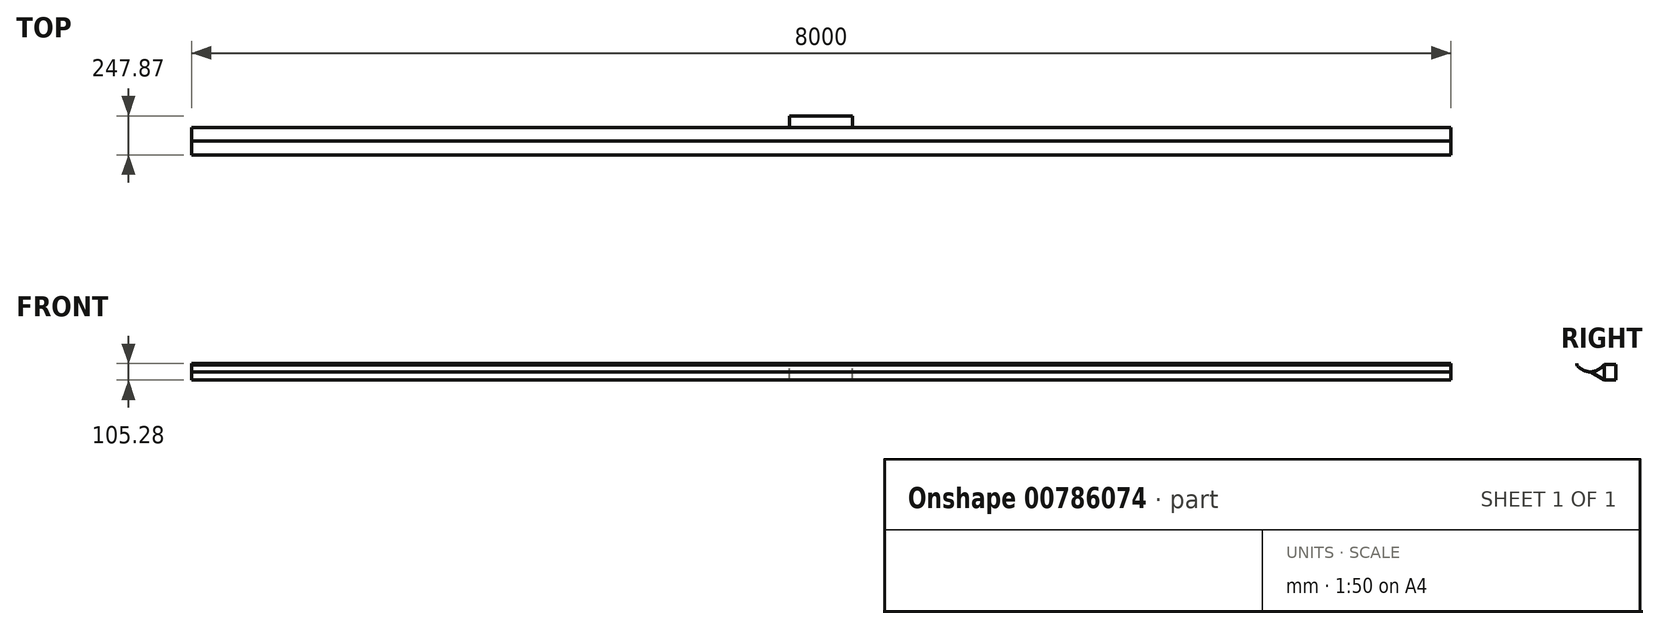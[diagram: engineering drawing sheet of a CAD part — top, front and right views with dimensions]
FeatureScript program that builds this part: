
annotation { "Feature Type Name" : "Feature", "Feature Type Description" : "" }
export const myFeature = defineFeature(function(context is Context, id is Id, definition is map)
    precondition{}
    {
        {
            var Q0;
            Q0=qCreatedBy(makeId("Right.planeOp"),FACE);
            var sketch = newSketch(context, id + "F0", { "sketchPlane" : qUnion([Q0])});
            skArc(sketch, "E0", {"start": v(-87.67, 11.49) * mm, "mid": v(0, -31.44) * mm, "end": v(85.2, 16.2) * mm});
            skLineSegment(sketch, "E1", {"start": v(-87.67, 11.49) * mm, "end": v(-87.67, 21.49) * mm});
            skLineSegment(sketch, "E2", {"start": v(0, -31.44) * mm, "end": v(85.2, -83.8) * mm});
            skLineSegment(sketch, "E3", {"start": v(85.2, -83.8) * mm, "end": v(85.2, 16.2) * mm});
            skLineSegment(sketch, "E4", {"start": v(0, -31.44) * mm, "end": v(85.2, -31.44) * mm});
            skPoint(sketch, "E4.endSnap0", {"position": v(85.2, -33.8) * mm});
            skLineSegment(sketch, "E5", {"start": v(41.06, -21.87) * mm, "end": v(41.06, -56.67) * mm});
            skLineSegment(sketch, "E6", {"start": v(54.68, -14.34) * mm, "end": v(54.68, -65.04) * mm});
            skLineSegment(sketch, "E7", {"start": v(66.2, -5.62) * mm, "end": v(66.2, -72.12) * mm});
            skLineSegment(sketch, "E8", {"start": v(85.2, -83.8) * mm, "end": v(160.2, -83.8) * mm});
            skLineSegment(sketch, "E9", {"start": v(110.2, -83.8) * mm, "end": v(110.2, 16.2) * mm});
            skLineSegment(sketch, "E10", {"start": v(135.2, -83.8) * mm, "end": v(135.2, 16.2) * mm});
            skLineSegment(sketch, "E11", {"start": v(160.2, -83.8) * mm, "end": v(160.2, 16.2) * mm});
            skLineSegment(sketch, "E12", {"start": v(85.2, 16.2) * mm, "end": v(110.2, 16.2) * mm});
            skLineSegment(sketch, "E13", {"start": v(135.2, 16.2) * mm, "end": v(110.2, 16.2) * mm});
            skLineSegment(sketch, "E14", {"start": v(160.2, 16.2) * mm, "end": v(135.2, 16.2) * mm});
            skLineSegment(sketch, "E15", {"start": v(76.2, 4.34) * mm, "end": v(76.2, -78.26) * mm});
            skLineSegment(sketch, "E16", {"start": v(85.2, -5.22) * mm, "end": v(110.2, -5.22) * mm});
            skLineSegment(sketch, "E17", {"start": v(110.2, -5.22) * mm, "end": v(123.7, -5.22) * mm});
            skLineSegment(sketch, "E18", {"start": v(123.7, -5.22) * mm, "end": v(123.7, -15.48) * mm});
            skLineSegment(sketch, "E19", {"start": v(123.7, -15.48) * mm, "end": v(160.2, -15.48) * mm});
            skLineSegment(sketch, "E20", {"start": v(123.7, -5.22) * mm, "end": v(123.7, 16.2) * mm});
            skLineSegment(sketch, "E21", {"start": v(85.2, 6.9) * mm, "end": v(123.7, 6.9) * mm});
            skLineSegment(sketch, "E22", {"start": v(160.2, -31.4) * mm, "end": v(85.2, -31.4) * mm});
            skLineSegment(sketch, "E23", {"start": v(123.7, -15.48) * mm, "end": v(85.2, -15.48) * mm});
            skLineSegment(sketch, "E24", {"start": v(85.2, -23.07) * mm, "end": v(160.2, -23.07) * mm});
            skLineSegment(sketch, "E25", {"start": v(85.2, -39.16) * mm, "end": v(160.2, -39.16) * mm});
            skLineSegment(sketch, "E26", {"start": v(85.2, -48.32) * mm, "end": v(160.2, -48.32) * mm});
            skLineSegment(sketch, "E27", {"start": v(85.2, -56.67) * mm, "end": v(160.2, -56.67) * mm});
            skLineSegment(sketch, "E28", {"start": v(85.2, -66.65) * mm, "end": v(160.2, -66.65) * mm});
            skLineSegment(sketch, "E29", {"start": v(85.2, -74.19) * mm, "end": v(160.2, -74.19) * mm});
            skSolve(sketch);
        }
        {
            var Q0;
            Q0=sQuery(id+"F0.wireOp",EDGE,"E2");
            extrude(context, id + "F1", {"bodyType" : ToolBodyType.SURFACE, "surfaceEntities" : qUnion([Q0]), "endBound" : BoundingType.SYMMETRIC, "depth" : 8000 * mm, "offsetDistance" : 25.4 * mm});
        }
        {
            var Q0;
            Q0=sQuery(id+"F0.wireOp",EDGE,"E0");
            var Q1;
            Q1=sQuery(id+"F0.wireOp",EDGE,"E1");
            extrude(context, id + "F2", {"bodyType" : ToolBodyType.SURFACE, "surfaceEntities" : qUnion([Q0, Q1]), "endBound" : BoundingType.SYMMETRIC, "depth" : 8000 * mm, "offsetDistance" : 25.4 * mm});
        }
        {
            var Q0;
            Q0=sQuery(id+"F0.wireOp",EDGE,"E12");
            var Q1;
            Q1=sQuery(id+"F0.wireOp",EDGE,"E13");
            var Q2;
            Q2=sQuery(id+"F0.wireOp",EDGE,"E14");
            var Q3;
            Q3=sQuery(id+"F0.wireOp",EDGE,"E11");
            var Q4;
            Q4=sQuery(id+"F0.wireOp",EDGE,"E8");
            extrude(context, id + "F3", {"bodyType" : ToolBodyType.SURFACE, "surfaceEntities" : qUnion([Q0, Q1, Q2, Q3, Q4]), "endBound" : BoundingType.SYMMETRIC, "depth" : 400 * mm, "offsetDistance" : 25.4 * mm});
        }
        {
            var Q0;
            Q0=sQuery(id+"F0.wireOp",EDGE,"E3");
            extrude(context, id + "F4", {"bodyType" : ToolBodyType.SURFACE, "surfaceEntities" : qUnion([Q0]), "endBound" : BoundingType.SYMMETRIC, "depth" : 8000 * mm, "offsetDistance" : 25.4 * mm});
        }
    });
